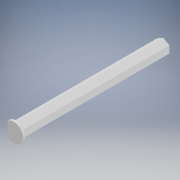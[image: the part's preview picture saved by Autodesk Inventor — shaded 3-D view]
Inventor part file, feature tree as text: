
AUTODESK INVENTOR PART (.ipt)
format: ipt  version: 2020 (Build 240168000, 168)  size: 246,272 bytes
history: native  units: in
note: dims shown in document units (in); Inventor stores cm internally (conversion verified against a paired STEP export)
features: extrude x2, sketch x2, projected_geometry x1
ambient origin geometry x8: Origin, YZ Plane, XZ Plane, XY Plane, X Axis, Y Axis, Z Axis, Center Point
bodies: Solid1 (feature_tree)
feature tree (5):
  extrude  "Extrusion1"  Depth=6.0in TaperAngle=0.0deg
  extrude  "Extrusion2"  Depth=0.1in TaperAngle=0.0deg
  sketch  "Sketch1"  dims[d0=0.5in d1=6.0in d2=0.0in]
  sketch  "Sketch2"  dims[d3=0.75in d4=0.1in d5=0.0in]
  projected_geometry  "Projected Loop1"
